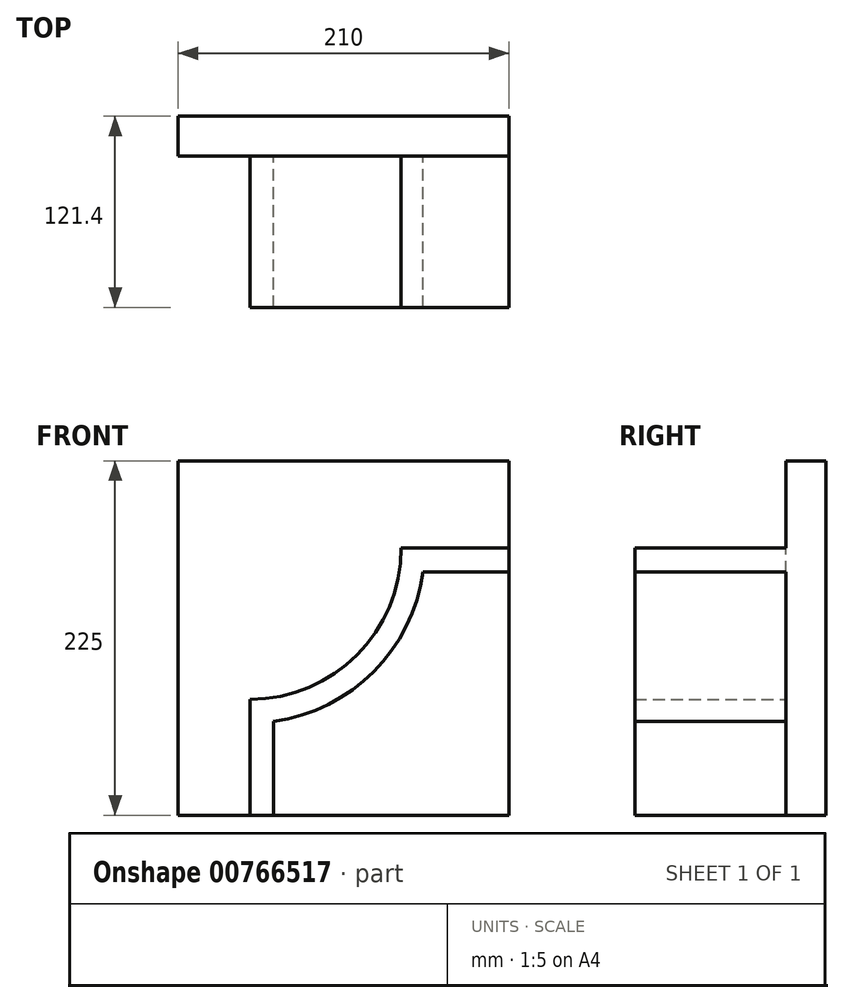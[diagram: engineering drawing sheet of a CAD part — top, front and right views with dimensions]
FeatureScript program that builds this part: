
annotation { "Feature Type Name" : "Feature", "Feature Type Description" : "" }
export const myFeature = defineFeature(function(context is Context, id is Id, definition is map)
    precondition{}
    {
        {
            var Q0;
            Q0=qCreatedBy(makeId("Front.planeOp"),FACE);
            var sketch = newSketch(context, id + "F0", { "sketchPlane" : qUnion([Q0])});
            skLineSegment(sketch, "E0.bottom", {"start": v(-130.3, 121.37) * mm, "end": v(79.7, 121.37) * mm});
            skLineSegment(sketch, "E0.top", {"start": v(-130.3, -103.63) * mm, "end": v(79.7, -103.63) * mm});
            skLineSegment(sketch, "E0.left", {"start": v(-130.3, 121.37) * mm, "end": v(-130.3, -103.63) * mm});
            skLineSegment(sketch, "E0.right", {"start": v(79.7, 121.37) * mm, "end": v(79.7, -103.63) * mm});
            skSolve(sketch);
        }
        {
            var Q0;
            Q0=makeQuery(id+"F0.imprint","IMPRINT",FACE,{"disambiguationData":[TD([[makeQuery(id+"F0.imprint","IMPRINT",EDGE,{"derivedFrom":sQuery(id+"F0.wireOp",EDGE,"E0.bottom")}),-1.0]])]});
            extrude(context, id + "F1", {"entities" : qUnion([Q0]), "depth" : 25.4 * mm, "offsetDistance" : 25.4 * mm});
        }
        {
            var Q0;
            Q0=makeQuery(id+"F1.opExtrude","SWEPT_BODY",BODY,{"disambiguationData":[OSD([sQuery(id+"F0.wireOp",EDGE,"E0.bottom"),sQuery(id+"F0.wireOp",EDGE,"E0.top"),sQuery(id+"F0.wireOp",EDGE,"E0.left"),sQuery(id+"F0.wireOp",EDGE,"E0.right")])]});
            transform(context, id + "F2", {"entities" : qUnion([Q0]), "transformType" : TransformType.TRANSLATION_3D, "dx" : 25.4 * mm, "dy" : 0 * mm, "dz" : -8.76 * mm, "makeCopy" : false});
        }
        {
            var Q0;
            Q0=makeQuery(id+"F1.opExtrude","CAP_FACE",FACE,{"disambiguationData":[OSD([sQuery(id+"F0.wireOp",EDGE,"E0.bottom"),sQuery(id+"F0.wireOp",EDGE,"E0.top"),sQuery(id+"F0.wireOp",EDGE,"E0.left"),sQuery(id+"F0.wireOp",EDGE,"E0.right")])],"isStart":false});
            var sketch = newSketch(context, id + "F3", { "sketchPlane" : qUnion([Q0])});
            skLineSegment(sketch, "E1", {"start": v(-59.32, -112.39) * mm, "end": v(-59.32, -38.76) * mm});
            skLineSegment(sketch, "E2", {"start": v(105.1, 57.24) * mm, "end": v(36.68, 57.24) * mm});
            skArc(sketch, "E3", {"start": v(-59.32, -38.76) * mm, "mid": v(8.56, -10.64) * mm, "end": v(36.68, 57.24) * mm});
            skLineSegment(sketch, "E4", {"start": v(-59.32, 57.24) * mm, "end": v(36.68, 57.24) * mm, "construction": true});
            skLineSegment(sketch, "E5", {"start": v(-59.32, 57.24) * mm, "end": v(-59.32, -38.76) * mm, "construction": true});
            skLineSegment(sketch, "E6.0", {"start": v(105.1, 42.24) * mm, "end": v(50.66, 42.24) * mm});
            skArc(sketch, "E6.1", {"start": v(-44.32, -52.74) * mm, "mid": v(19.17, -21.25) * mm, "end": v(50.66, 42.24) * mm});
            skLineSegment(sketch, "E6.2", {"start": v(-44.32, -112.83) * mm, "end": v(-44.32, -52.74) * mm});
            skLineSegment(sketch, "E7.0.0", {"start": v(-104.9, 112.61) * mm, "end": v(-104.9, -112.39) * mm});
            skLineSegment(sketch, "E7.0.1", {"start": v(-104.9, -112.39) * mm, "end": v(105.1, -112.39) * mm});
            skLineSegment(sketch, "E7.0.2", {"start": v(105.1, -112.39) * mm, "end": v(105.1, 112.61) * mm});
            skLineSegment(sketch, "E7.0.3", {"start": v(105.1, 112.61) * mm, "end": v(-104.9, 112.61) * mm});
            skLineSegment(sketch, "E8", {"start": v(-59.32, -112.39) * mm, "end": v(-59.32, 57.24) * mm});
            skLineSegment(sketch, "E9", {"start": v(-59.32, 57.24) * mm, "end": v(105.1, 57.24) * mm});
            skSolve(sketch);
        }
        {
            var Q0;
            {var subQ6=sQuery(id+"F3.wireOp",EDGE,"E3");Q0=makeQuery(id+"F3.imprint","IMPRINT",FACE,{"disambiguationData":[TD([[makeQuery(id+"F3.imprint","IMPRINT",EDGE,{"derivedFrom":subQ6}),-1.0]])]});}
            extrude(context, id + "F4", {"entities" : qUnion([Q0]), "operationType" : NewBodyOperationType.ADD, "depth" : 96 * mm, "offsetDistance" : 25.4 * mm});
        }
    });
